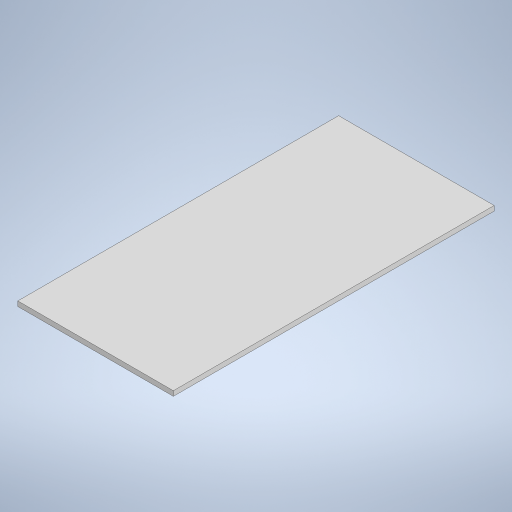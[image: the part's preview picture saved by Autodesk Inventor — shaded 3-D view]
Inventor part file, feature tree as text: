
AUTODESK INVENTOR PART (.ipt)
format: ipt  version: 2023 (Build 270158000, 158)  size: 203,776 bytes
history: native  units: in
note: dims shown in document units (in); Inventor stores cm internally (conversion verified against a paired STEP export)
features: extrude x1, sketch x1
ambient origin geometry x8: Origin, YZ Plane, XZ Plane, XY Plane, X Axis, Y Axis, Z Axis, Center Point
bodies: Solid1 (feature_tree)
feature tree (2):
  extrude  "Extrusion1"  Depth=16.5in
  sketch  "Sketch1"  dims[d0=8.0in d1=16.5in d2=0.25in d3=0.0in]
